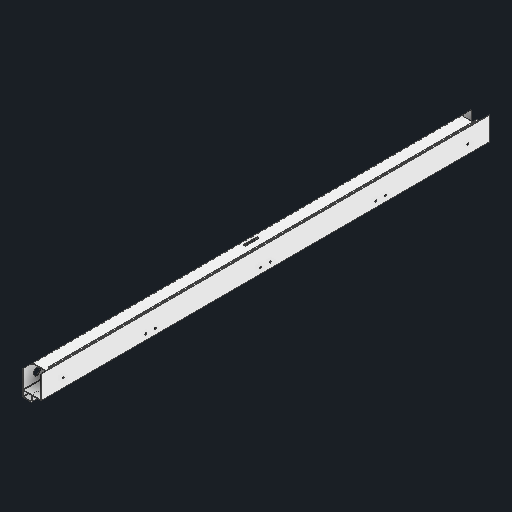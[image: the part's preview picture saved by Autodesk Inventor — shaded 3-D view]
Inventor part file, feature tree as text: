
AUTODESK INVENTOR PART (.ipt)
format: ipt  version: 2024.2 (Build 282272000, 272)  size: 192,512 bytes
history: native  units: in
note: dims shown in document units (in); Inventor stores cm internally (conversion verified against a paired STEP export)
features: fillet x1
ambient origin geometry x8: Origin, YZ Plane, XZ Plane, XY Plane, X Axis, Y Axis, Z Axis, Center Point
bodies: Solid1 (feature_tree)
feature tree (1):
  fillet  "Fillet13"  [1 undecoded]
note: 1 required parameter value undecoded (feature->parameter linkage not recoverable at this tier; creation-order binding heuristic only, values carry confidence <= 0.55)
